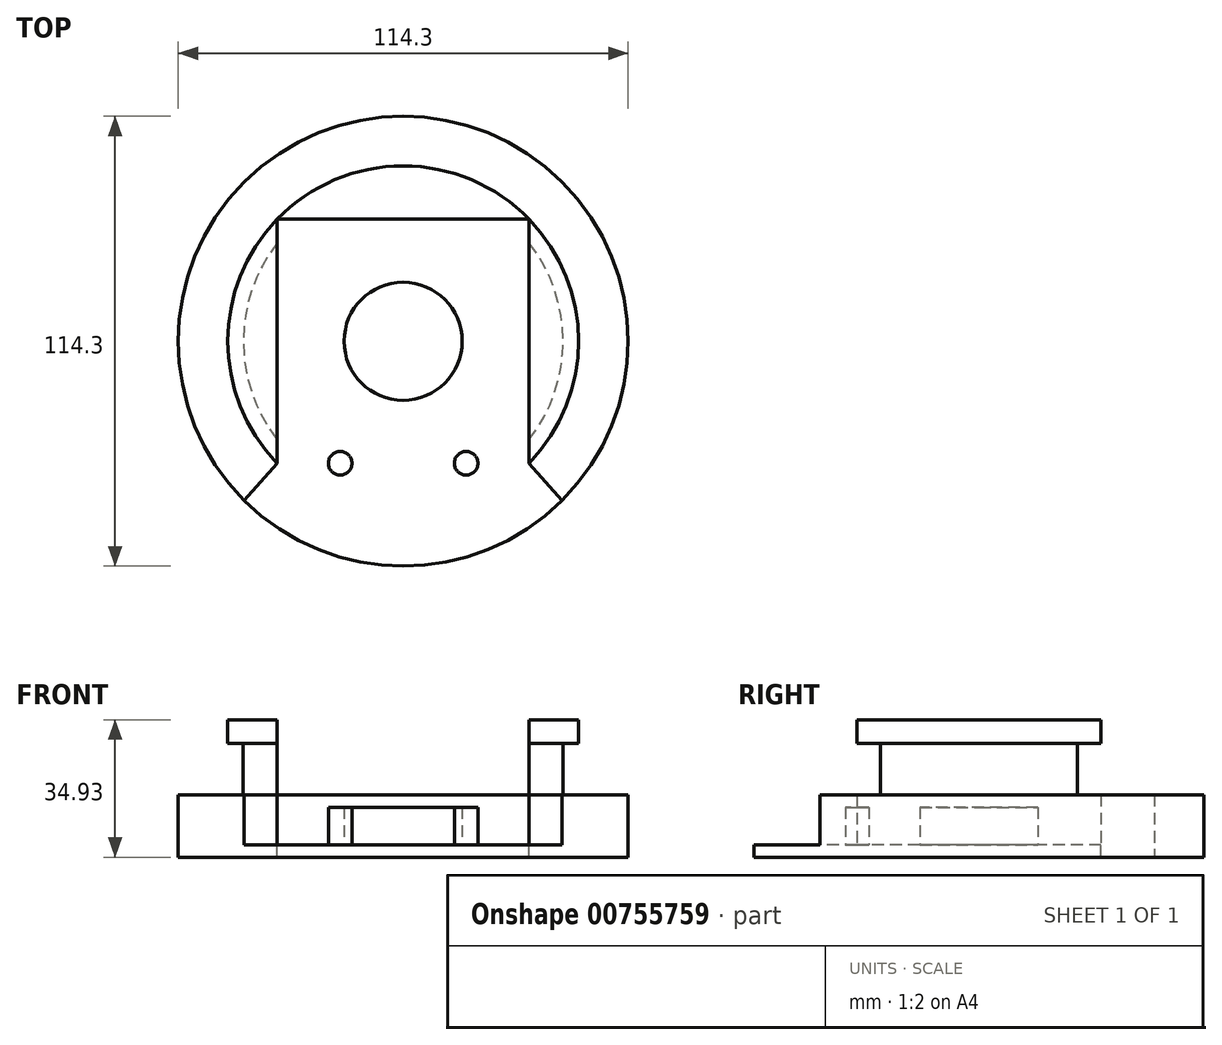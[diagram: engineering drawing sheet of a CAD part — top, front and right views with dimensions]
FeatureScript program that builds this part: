
annotation { "Feature Type Name" : "Feature", "Feature Type Description" : "" }
export const myFeature = defineFeature(function(context is Context, id is Id, definition is map)
    precondition{}
    {
        {
            assignVariable(context, id + "F0", {"name" : "Thickness", "anyValue" : 12.7 * mm});
        }
        {
            var Q0;
            Q0=qCreatedBy(makeId("Top.planeOp"),FACE);
            var sketch = newSketch(context, id + "F1", { "sketchPlane" : qUnion([Q0])});
            skCircle(sketch, "E0", {"center": v(0, 0) * mm, "radius": 57.15 * mm});
            skLineSegment(sketch, "E1", {"start": v(-32, 31) * mm, "end": v(-32, -31) * mm});
            skPoint(sketch, "E2", {"position": v(-32, 0) * mm});
            skArc(sketch, "E3", {"start": v(-32, 31) * mm, "mid": v(-44.55, 0) * mm, "end": v(-32, -31) * mm});
            skLineSegment(sketch, "E4.MirrorCS", {"start": v(32, 31) * mm, "end": v(32, -31) * mm});
            skArc(sketch, "E5.MirrorCS", {"start": v(32, 31) * mm, "mid": v(44.55, 0) * mm, "end": v(32, -31) * mm});
            skLineSegment(sketch, "E6", {"start": v(0, 31) * mm, "end": v(0, -31) * mm, "construction": true});
            skArc(sketch, "E7", {"start": v(-32, 31) * mm, "mid": v(0, 44.55) * mm, "end": v(32, 31) * mm});
            skCircle(sketch, "E8", {"center": v(0, 0) * mm, "radius": 15 * mm});
            skLineSegment(sketch, "E9", {"start": v(-32, -31) * mm, "end": v(0, -31) * mm, "construction": true});
            skLineSegment(sketch, "E10", {"start": v(32, -31) * mm, "end": v(0, -31) * mm, "construction": true});
            skPoint(sketch, "E11", {"position": v(-16, -31) * mm});
            skPoint(sketch, "E12", {"position": v(16, -31) * mm});
            skCircle(sketch, "E13", {"center": v(-16, -31) * mm, "radius": 3 * mm});
            skCircle(sketch, "E14", {"center": v(16, -31) * mm, "radius": 3 * mm});
            skLineSegment(sketch, "E15", {"start": v(0, 0) * mm, "end": v(40.41, -40.41) * mm, "construction": true});
            skLineSegment(sketch, "E16", {"start": v(0, 0) * mm, "end": v(-40.41, -40.41) * mm, "construction": true});
            skLineSegment(sketch, "E17", {"start": v(-32, -31) * mm, "end": v(-40.41, -40.41) * mm});
            skLineSegment(sketch, "E18", {"start": v(32, -31) * mm, "end": v(40.41, -40.41) * mm});
            skLineSegment(sketch, "E19", {"start": v(32, 31) * mm, "end": v(-32, 31) * mm});
            skSolve(sketch);
        }
        {
            var Q0;
            Q0=makeQuery(id+"F1.imprint","IMPRINT",FACE,{"disambiguationData":[TD([[makeQuery(id+"F1.imprint","IMPRINT",EDGE,{"derivedFrom":sQuery(id+"F1.wireOp",EDGE,"E1")}),-1.0]])]});
            var Q1;
            Q1=makeQuery(id+"F1.imprint","IMPRINT",FACE,{"disambiguationData":[TD([[makeQuery(id+"F1.imprint","IMPRINT",EDGE,{"derivedFrom":sQuery(id+"F1.wireOp",EDGE,"E4.MirrorCS")}),1.0]])]});
            extrude(context, id + "F2", {"entities" : qUnion([Q0, Q1]), "depth" : getVariable(context, 'Thickness') * 2.5, "offsetDistance" : 25 * mm});
        }
        {
            var Q0;
            Q0=makeQuery(id+"F1.imprint","IMPRINT",FACE,{"disambiguationData":[TD([[makeQuery(id+"F1.imprint","IMPRINT",EDGE,{"derivedFrom":sQuery(id+"F1.wireOp",EDGE,"E3")}),-1.0]])]});
            var Q1;
            Q1=makeQuery(id+"F1.imprint","IMPRINT",FACE,{"disambiguationData":[TD([[makeQuery(id+"F1.imprint","IMPRINT",EDGE,{"derivedFrom":sQuery(id+"F1.wireOp",EDGE,"E7")}),-1.0]])]});
            extrude(context, id + "F3", {"entities" : qUnion([Q0, Q1]), "depth" : getVariable(context, 'Thickness'), "offsetDistance" : 25 * mm});
        }
        {
            var Q0;
            Q0=makeQuery(id+"F1.imprint","IMPRINT",FACE,{"disambiguationData":[TD([[makeQuery(id+"F1.imprint","IMPRINT",EDGE,{"derivedFrom":sQuery(id+"F1.wireOp",EDGE,"E8")}),1.0]])]});
            var Q1;
            Q1=makeQuery(id+"F1.imprint","IMPRINT",FACE,{"disambiguationData":[TD([[makeQuery(id+"F1.imprint","IMPRINT",EDGE,{"derivedFrom":sQuery(id+"F1.wireOp",EDGE,"E14")}),1.0]])]});
            var Q2;
            Q2=makeQuery(id+"F1.imprint","IMPRINT",FACE,{"disambiguationData":[TD([[makeQuery(id+"F1.imprint","IMPRINT",EDGE,{"derivedFrom":sQuery(id+"F1.wireOp",EDGE,"E13")}),1.0]])]});
            extrude(context, id + "F4", {"entities" : qUnion([Q0, Q1, Q2]), "depth" : getVariable(context, 'Thickness') * 0.75, "offsetDistance" : 25 * mm});
        }
        {
            var Q0;
            Q0=makeQuery(id+"F1.imprint","IMPRINT",FACE,{"disambiguationData":[TD([[makeQuery(id+"F1.imprint","IMPRINT",EDGE,{"derivedFrom":sQuery(id+"F1.wireOp",EDGE,"E1")}),1.0]])]});
            var Q1;
            Q1=makeQuery(id+"F1.imprint","IMPRINT",FACE,{"disambiguationData":[TD([[makeQuery(id+"F1.imprint","IMPRINT",EDGE,{"derivedFrom":sQuery(id+"F1.wireOp",EDGE,"E3")}),-1.0]])]});
            var Q2;
            Q2=makeQuery(id+"F1.imprint","IMPRINT",FACE,{"disambiguationData":[TD([[makeQuery(id+"F1.imprint","IMPRINT",EDGE,{"derivedFrom":sQuery(id+"F1.wireOp",EDGE,"E4.MirrorCS")}),1.0]])]});
            var Q3;
            Q3=makeQuery(id+"F1.imprint","IMPRINT",FACE,{"disambiguationData":[TD([[makeQuery(id+"F1.imprint","IMPRINT",EDGE,{"derivedFrom":sQuery(id+"F1.wireOp",EDGE,"E7")}),-1.0]])]});
            var Q4;
            Q4=makeQuery(id+"F1.imprint","IMPRINT",FACE,{"disambiguationData":[TD([[makeQuery(id+"F1.imprint","IMPRINT",EDGE,{"derivedFrom":sQuery(id+"F1.wireOp",EDGE,"E1")}),-1.0]])]});
            var Q5;
            Q5=makeQuery(id+"F1.imprint","IMPRINT",FACE,{"disambiguationData":[TD([[makeQuery(id+"F1.imprint","IMPRINT",EDGE,{"derivedFrom":sQuery(id+"F1.wireOp",EDGE,"E13")}),1.0]])]});
            var Q6;
            Q6=makeQuery(id+"F1.imprint","IMPRINT",FACE,{"disambiguationData":[TD([[makeQuery(id+"F1.imprint","IMPRINT",EDGE,{"derivedFrom":sQuery(id+"F1.wireOp",EDGE,"E14")}),1.0]])]});
            var Q7;
            Q7=makeQuery(id+"F1.imprint","IMPRINT",FACE,{"disambiguationData":[TD([[makeQuery(id+"F1.imprint","IMPRINT",EDGE,{"derivedFrom":sQuery(id+"F1.wireOp",EDGE,"E8")}),1.0]])]});
            extrude(context, id + "F5", {"entities" : qUnion([Q0, Q1, Q2, Q3, Q4, Q5, Q6, Q7]), "operationType" : NewBodyOperationType.ADD, "oppositeDirection" : true, "depth" : getVariable(context, 'Thickness') / 4, "offsetDistance" : 25 * mm});
        }
        {
            var Q0;
            Q0=makeQuery(id+"F2.opExtrude","SWEPT_FACE",FACE,{"disambiguationData":[OSD([sQuery(id+"F1.wireOp",EDGE,"E1")])]});
            var sketch = newSketch(context, id + "F6", { "sketchPlane" : qUnion([Q0])});
            skLineSegment(sketch, "E20.bottom", {"start": v(-31, 12.7) * mm, "end": v(-25, 12.7) * mm});
            skLineSegment(sketch, "E20.top", {"start": v(-31, 25.75) * mm, "end": v(-25, 25.75) * mm});
            skLineSegment(sketch, "E20.left", {"start": v(-31, 12.7) * mm, "end": v(-31, 25.75) * mm});
            skLineSegment(sketch, "E20.right", {"start": v(-25, 12.7) * mm, "end": v(-25, 25.75) * mm});
            skSolve(sketch);
        }
        {
            var Q0;
            Q0=makeQuery(id+"F6.imprint","IMPRINT",FACE,{"disambiguationData":[TD([[makeQuery(id+"F6.imprint","IMPRINT",EDGE,{"derivedFrom":sQuery(id+"F6.wireOp",EDGE,"E20.bottom")}),1.0]])]});
            var Q1;
            Q1=makeQuery(id+"F4.opExtrude","SWEPT_FACE",FACE,{"disambiguationData":[OSD([sQuery(id+"F1.wireOp",EDGE,"E8")])]});
            revolve(context, id + "F7", {"operationType" : NewBodyOperationType.REMOVE, "surfaceOperationType" : NewSurfaceOperationType.NEW, "entities" : qUnion([Q0]), "axis" : qUnion([Q1]), "revolveType" : RevolveType.FULL, "oppositeDirection" : true});
        }
    });
